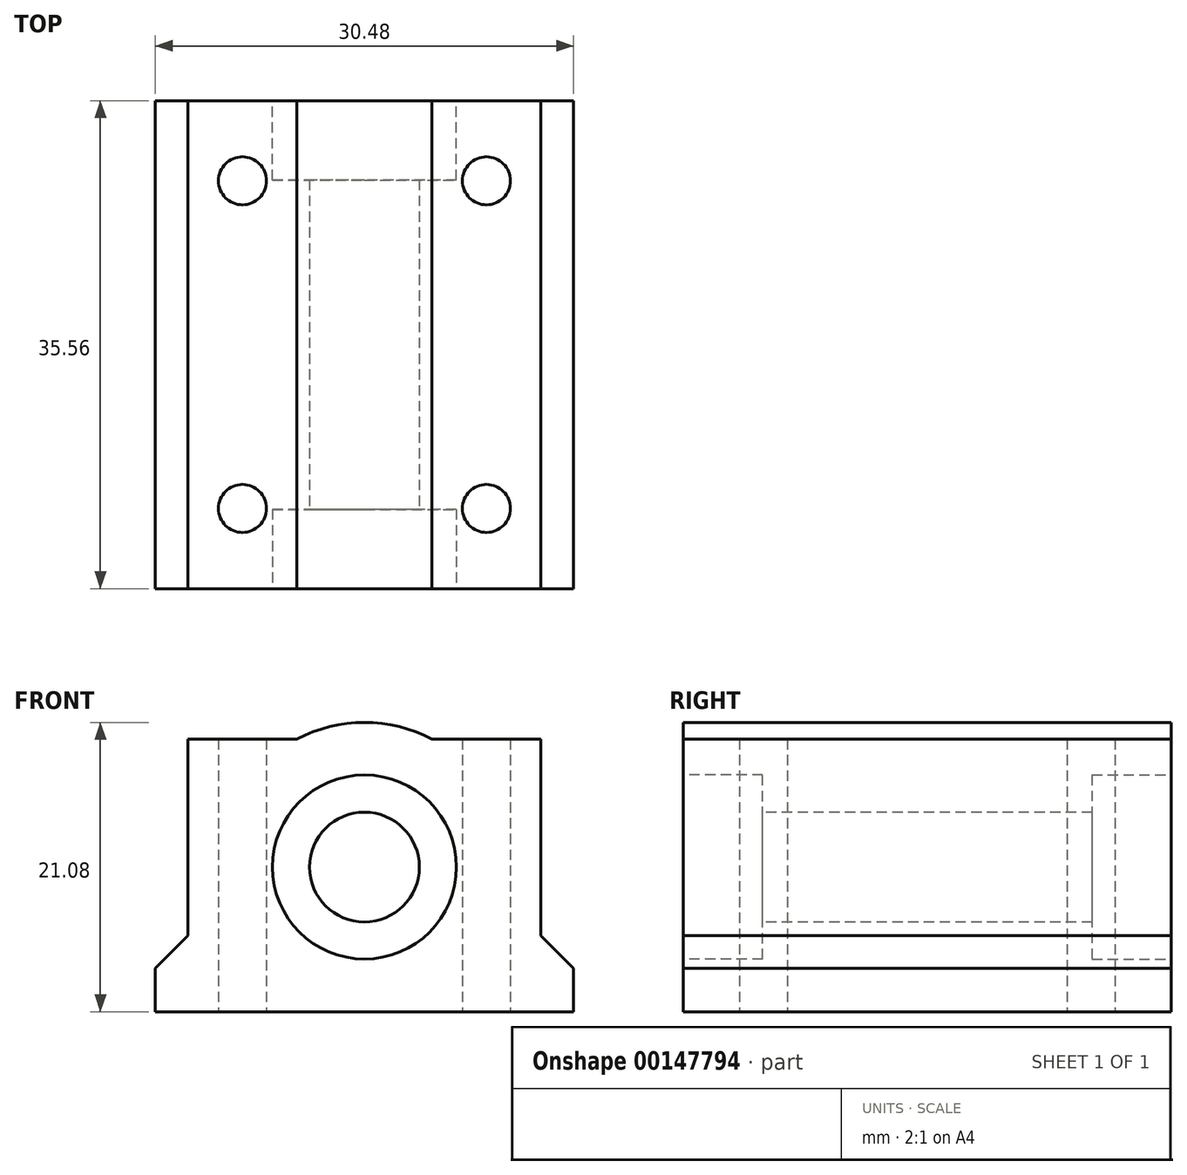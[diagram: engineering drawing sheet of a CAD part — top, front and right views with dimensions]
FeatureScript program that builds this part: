
annotation { "Feature Type Name" : "Feature", "Feature Type Description" : "" }
export const myFeature = defineFeature(function(context is Context, id is Id, definition is map)
    precondition{}
    {
        {
            var Q0;
            Q0=qCreatedBy(makeId("Top.planeOp"),FACE);
            var sketch = newSketch(context, id + "F0", { "sketchPlane" : qUnion([Q0])});
            skLineSegment(sketch, "E0.bottom", {"start": v(0, 0) * mm, "end": v(30.48, 0) * mm});
            skLineSegment(sketch, "E0.top", {"start": v(0, -35.56) * mm, "end": v(30.48, -35.56) * mm});
            skLineSegment(sketch, "E0.left", {"start": v(0, 0) * mm, "end": v(0, -35.56) * mm});
            skLineSegment(sketch, "E0.right", {"start": v(30.48, 0) * mm, "end": v(30.48, -35.56) * mm});
            skLineSegment(sketch, "E1", {"start": v(15.24, 0) * mm, "end": v(15.24, -35.56) * mm, "construction": true});
            skLineSegment(sketch, "E2.bottom", {"start": v(6.35, -5.84) * mm, "end": v(24.13, -5.84) * mm, "construction": true});
            skLineSegment(sketch, "E2.top", {"start": v(6.35, -29.72) * mm, "end": v(24.13, -29.72) * mm, "construction": true});
            skLineSegment(sketch, "E2.left", {"start": v(6.35, -5.84) * mm, "end": v(6.35, -29.72) * mm, "construction": true});
            skLineSegment(sketch, "E2.right", {"start": v(24.13, -5.84) * mm, "end": v(24.13, -29.72) * mm, "construction": true});
            skPoint(sketch, "E2.middle", {"position": v(15.24, -17.78) * mm});
            skCircle(sketch, "E3", {"center": v(6.35, -5.84) * mm, "radius": 1.75 * mm});
            skCircle(sketch, "E4", {"center": v(24.13, -5.84) * mm, "radius": 1.75 * mm});
            skCircle(sketch, "E5", {"center": v(24.13, -29.72) * mm, "radius": 1.75 * mm});
            skCircle(sketch, "E6", {"center": v(6.35, -29.72) * mm, "radius": 1.75 * mm});
            skSolve(sketch);
        }
        {
            var Q0;
            Q0=qSketchRegion(id+"F0",true);
            extrude(context, id + "F1", {"entities" : qUnion([Q0]), "depth" : 21.08 * mm});
        }
        {
            var Q0;
            Q0=makeQuery(id+"F1.opExtrude","SWEPT_FACE",FACE,{"disambiguationData":[OSD([sQuery(id+"F0.wireOp",EDGE,"E0.top")])]});
            var sketch = newSketch(context, id + "F2", { "sketchPlane" : qUnion([Q0])});
            skLineSegment(sketch, "E7", {"start": v(15.24, 21.08) * mm, "end": v(15.24, 0) * mm, "construction": true});
            skCircle(sketch, "E8", {"center": v(15.24, 10.54) * mm, "radius": 4 * mm});
            skArc(sketch, "E9", {"start": v(20.16, 19.86) * mm, "mid": v(15.24, 21.08) * mm, "end": v(10.32, 19.86) * mm});
            skLineSegment(sketch, "E10", {"start": v(24.13, 21.08) * mm, "end": v(24.13, 19.86) * mm, "construction": true});
            skLineSegment(sketch, "E11", {"start": v(20.16, 19.86) * mm, "end": v(28.1, 19.86) * mm});
            skLineSegment(sketch, "E12", {"start": v(28.1, 19.86) * mm, "end": v(28.1, 5.56) * mm});
            skLineSegment(sketch, "E13", {"start": v(28.1, 5.56) * mm, "end": v(30.48, 3.18) * mm});
            skLineSegment(sketch, "E14", {"start": v(30.48, 3.18) * mm, "end": v(30.48, 21.08) * mm});
            skLineSegment(sketch, "E15", {"start": v(30.48, 21.08) * mm, "end": v(15.24, 21.08) * mm});
            skLineSegment(sketch, "E16", {"start": v(10.32, 19.86) * mm, "end": v(2.38, 19.86) * mm});
            skLineSegment(sketch, "E17", {"start": v(2.38, 19.86) * mm, "end": v(2.38, 5.56) * mm});
            skLineSegment(sketch, "E18", {"start": v(2.38, 5.56) * mm, "end": v(0, 3.17) * mm});
            skLineSegment(sketch, "E19", {"start": v(15.24, 21.08) * mm, "end": v(0, 21.08) * mm});
            skLineSegment(sketch, "E20", {"start": v(0, 21.08) * mm, "end": v(0, 3.17) * mm});
            skSolve(sketch);
        }
        {
            var Q0;
            Q0=qSketchRegion(id+"F2",true);
            var Q1;
            Q1=makeQuery(id+"F1.opExtrude","SWEPT_FACE",FACE,{"disambiguationData":[OSD([sQuery(id+"F0.wireOp",EDGE,"E0.bottom")])]});
            extrude(context, id + "F3", {"entities" : qUnion([Q0]), "operationType" : NewBodyOperationType.REMOVE, "endBound" : BoundingType.UP_TO_SURFACE, "oppositeDirection" : true, "endBoundEntityFace" : qUnion([Q1]), "depth" : 25.4 * mm});
        }
        {
            var Q0;
            Q0=makeQuery(id+"F1.opExtrude","SWEPT_FACE",FACE,{"disambiguationData":[OSD([sQuery(id+"F0.wireOp",EDGE,"E0.top")])]});
            var sketch = newSketch(context, id + "F4", { "sketchPlane" : qUnion([Q0])});
            skCircle(sketch, "E21", {"center": v(15.24, 10.54) * mm, "radius": 6.7 * mm});
            skSolve(sketch);
        }
        {
            var Q0;
            Q0=qSketchRegion(id+"F4",true);
            extrude(context, id + "F5", {"entities" : qUnion([Q0]), "operationType" : NewBodyOperationType.REMOVE, "oppositeDirection" : true, "depth" : 5.78 * mm});
        }
        {
            var Q0;
            Q0=makeQuery(id+"F1.opExtrude","SWEPT_FACE",FACE,{"disambiguationData":[OSD([sQuery(id+"F0.wireOp",EDGE,"E0.bottom")])]});
            var sketch = newSketch(context, id + "F6", { "sketchPlane" : qUnion([Q0])});
            skCircle(sketch, "E22", {"center": v(-15.24, 10.54) * mm, "radius": 6.7 * mm});
            skSolve(sketch);
        }
        {
            var Q0;
            Q0=qSketchRegion(id+"F6",true);
            extrude(context, id + "F7", {"entities" : qUnion([Q0]), "operationType" : NewBodyOperationType.REMOVE, "oppositeDirection" : true, "depth" : 5.78 * mm});
        }
    });
